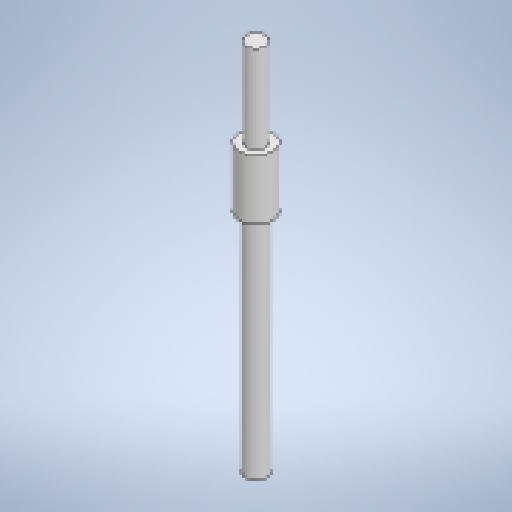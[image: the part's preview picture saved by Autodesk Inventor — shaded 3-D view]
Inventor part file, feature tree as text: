
AUTODESK INVENTOR PART (.ipt)
format: ipt  version: 2025.1 (Build 291241020, 241B)  size: 162,304 bytes
history: native  units: mm
features: sketch x2, revolve x1, plane x1, extrude x1, projected_geometry x1
ambient origin geometry x8: Origin, YZ Plane, XZ Plane, XY Plane, X Axis, Y Axis, Z Axis, Center Point
bodies: Body1 (feature_tree)
feature tree (6):
  revolve  "Revolution1"  [1 undecoded]
  plane  "Work Plane1"
  extrude  "Extrusion2"  Depth=10.0mm
  sketch  "Sketch2"  dims[d3=90.0deg d4=10.0mm d5=0.0mm]
  sketch  "Sketch3"  dims[d6=30.0mm d8=12.0mm d9=8.0mm d10=10.0mm d11=308.0mm d12=85.0mm d13=120.0mm d14=38.0mm d15=25.0mm]
  projected_geometry  "Projected Loop1"
note: 1 required parameter value undecoded (feature->parameter linkage not recoverable at this tier; creation-order binding heuristic only, values carry confidence <= 0.55)
